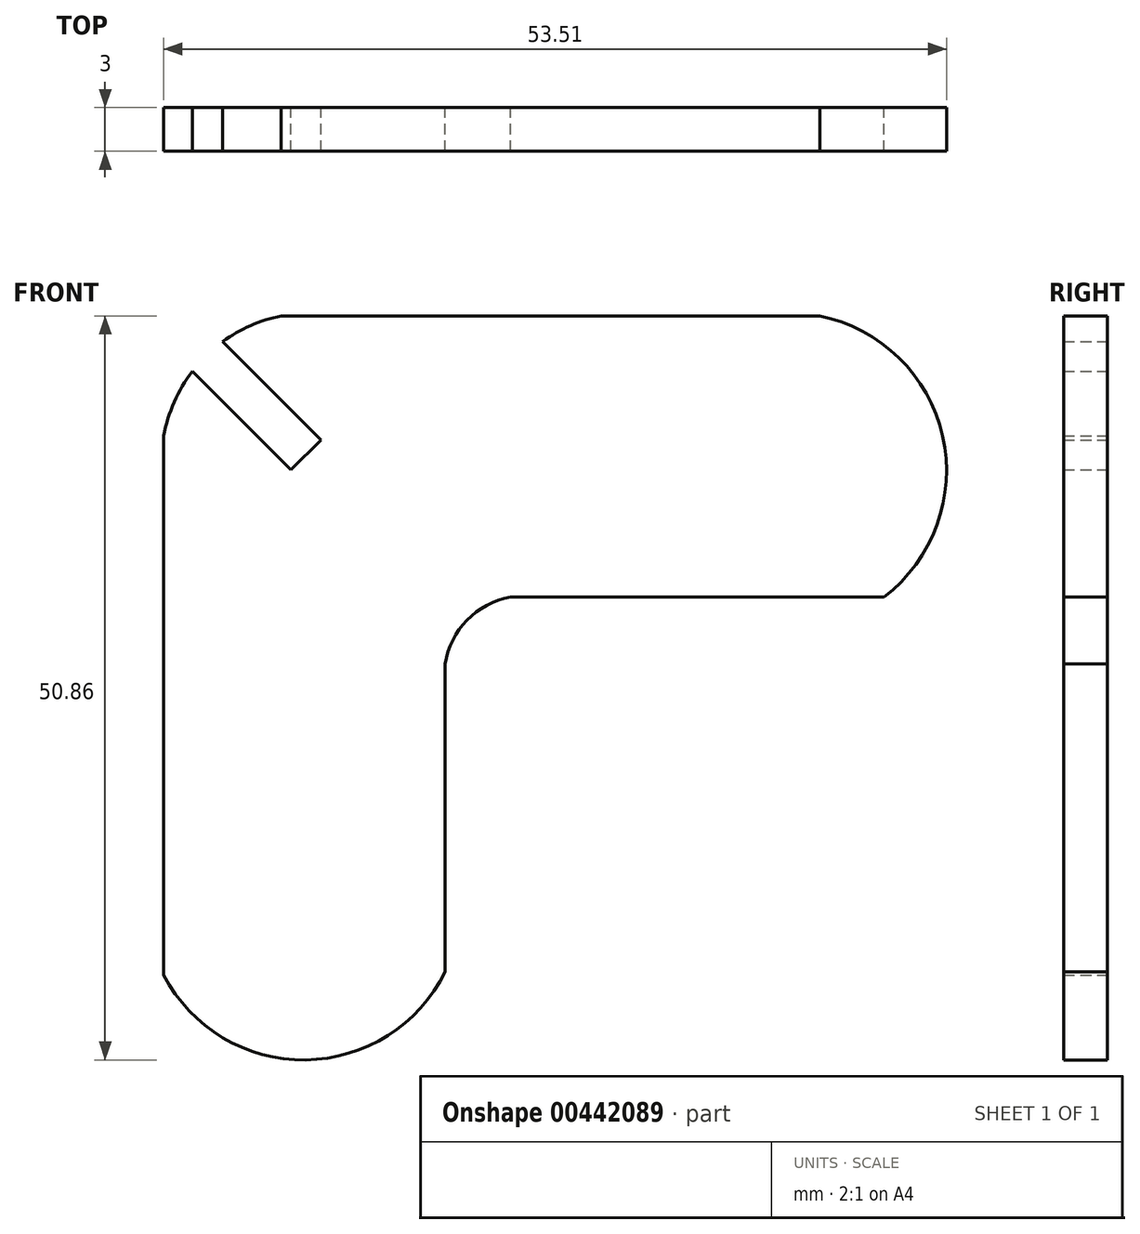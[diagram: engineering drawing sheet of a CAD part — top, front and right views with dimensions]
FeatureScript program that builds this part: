
annotation { "Feature Type Name" : "Feature", "Feature Type Description" : "" }
export const myFeature = defineFeature(function(context is Context, id is Id, definition is map)
    precondition{}
    {
        {
            var Q0;
            Q0=qCreatedBy(makeId("Front.planeOp"),FACE);
            var sketch = newSketch(context, id + "F0", { "sketchPlane" : qUnion([Q0])});
            skLineSegment(sketch, "E0.bottom", {"start": v(-14.18, 20.35) * mm, "end": v(-2.98, 20.35) * mm});
            skLineSegment(sketch, "E0.right", {"start": v(-2.98, 20.35) * mm, "end": v(-2.98, -24.5) * mm});
            skLineSegment(sketch, "E1.bottom", {"start": v(-14.18, 20.35) * mm, "end": v(22.64, 20.35) * mm});
            skLineSegment(sketch, "E1.top", {"start": v(-22.2, 1.12) * mm, "end": v(27.01, 1.12) * mm});
            skLineSegment(sketch, "E1.left", {"start": v(-22.2, 12.14) * mm, "end": v(-22.2, 1.12) * mm});
            skArc(sketch, "E2", {"start": v(-22.2, -24.72) * mm, "mid": v(-12.52, -30.5) * mm, "end": v(-2.98, -24.5) * mm});
            skArc(sketch, "E3", {"start": v(27.01, 1.12) * mm, "mid": v(31.03, 12.15) * mm, "end": v(22.64, 20.35) * mm});
            skPoint(sketch, "E4.middle", {"position": v(-22.2, 20.35) * mm});
            skLineSegment(sketch, "E5", {"start": v(-2.98, 20.35) * mm, "end": v(-22.2, 1.12) * mm});
            skLineSegment(sketch, "E6.bottom", {"start": v(-18.18, 18.6) * mm, "end": v(-0.7, 1.12) * mm});
            skLineSegment(sketch, "E6.top", {"start": v(-20.26, 16.57) * mm, "end": v(-2.98, -0.71) * mm});
            skPoint(sketch, "E6.middle", {"position": v(-14.37, 12.74) * mm});
            skArc(sketch, "E7", {"start": v(-14.18, 20.35) * mm, "mid": v(-16.28, 19.69) * mm, "end": v(-18.18, 18.6) * mm});
            skPoint(sketch, "E6.left.end.orphan", {"position": v(-30.19, 26.5) * mm});
            skPoint(sketch, "E6.left.start.orphan", {"position": v(-28.14, 28.55) * mm});
            skLineSegment(sketch, "E8.trimOffspring", {"start": v(-22.2, 12.14) * mm, "end": v(-22.2, -24.72) * mm});
            skArc(sketch, "E9.trimOffspring", {"start": v(-20.26, 16.57) * mm, "mid": v(-21.5, 14.47) * mm, "end": v(-22.2, 12.14) * mm});
            skPoint(sketch, "E6.right.end.orphan", {"position": v(-0.6, -3.08) * mm});
            skPoint(sketch, "E6.right.start.orphan", {"position": v(1.44, -1.03) * mm});
            skArc(sketch, "E10", {"start": v(3.42, 1.12) * mm, "mid": v(-1.38, -0.36) * mm, "end": v(-2.98, -5.13) * mm});
            skSolve(sketch);
        }
        {
            var Q0;
            {var subQ0=sQuery(id+"F0.wireOp",EDGE,"E2");Q0=makeQuery(id+"F0.imprint","IMPRINT",FACE,{"disambiguationData":[TD([[makeQuery(id+"F0.imprint","IMPRINT",EDGE,{"derivedFrom":subQ0}),1.0]])]});}
            var Q1;
            {var subQ5=sQuery(id+"F0.wireOp",EDGE,"E9.trimOffspring");Q1=makeQuery(id+"F0.imprint","IMPRINT",FACE,{"disambiguationData":[TD([[makeQuery(id+"F0.imprint","IMPRINT",EDGE,{"derivedFrom":subQ5}),1.0]])]});}
            var Q2;
            {var subQ0=sQuery(id+"F0.wireOp",EDGE,"E5");var subQ3=sQuery(id+"F0.wireOp",EDGE,"E6.bottom");var subQ5=makeQuery(id+"F0.imprint","INTERSECT",VERTEX,{"derivedFrom":[subQ0,subQ3]});Q2=makeQuery(id+"F0.imprint","IMPRINT",FACE,{"disambiguationData":[TD([[makeQuery(id+"F0.imprint","IMPRINT",EDGE,{"disambiguationData":[TD([[subQ5,-1.0]])],"derivedFrom":subQ3}),1.0]])]});}
            var Q3;
            {var subQ0=sQuery(id+"F0.wireOp",EDGE,"E5");var subQ3=sQuery(id+"F0.wireOp",EDGE,"E6.top");var subQ5=makeQuery(id+"F0.imprint","INTERSECT",VERTEX,{"derivedFrom":[subQ0,subQ3]});Q3=makeQuery(id+"F0.imprint","IMPRINT",FACE,{"disambiguationData":[TD([[makeQuery(id+"F0.imprint","IMPRINT",EDGE,{"disambiguationData":[TD([[subQ5,-1.0]])],"derivedFrom":subQ3}),-1.0]])]});}
            var Q4;
            {var subQ0=sQuery(id+"F0.wireOp",EDGE,"E3");Q4=makeQuery(id+"F0.imprint","IMPRINT",FACE,{"disambiguationData":[TD([[makeQuery(id+"F0.imprint","IMPRINT",EDGE,{"derivedFrom":subQ0}),1.0]])]});}
            var Q5;
            {var subQ3=sQuery(id+"F0.wireOp",EDGE,"E7");Q5=makeQuery(id+"F0.imprint","IMPRINT",FACE,{"disambiguationData":[TD([[makeQuery(id+"F0.imprint","IMPRINT",EDGE,{"derivedFrom":subQ3}),1.0]])]});}
            var Q6;
            {var subQ0=sQuery(id+"F0.wireOp",EDGE,"E6.bottom");var subQ3=sQuery(id+"F0.wireOp",EDGE,"E0.right");var subQ4=makeQuery(id+"F0.imprint","INTERSECT",VERTEX,{"derivedFrom":[subQ3,subQ0]});Q6=makeQuery(id+"F0.imprint","IMPRINT",FACE,{"disambiguationData":[TD([[makeQuery(id+"F0.imprint","IMPRINT",EDGE,{"disambiguationData":[TD([[subQ4,-1.0]])],"derivedFrom":subQ3}),-1.0]])]});}
            var Q7;
            {var subQ0=sQuery(id+"F0.wireOp",EDGE,"E6.top");var subQ1=sQuery(id+"F0.wireOp",EDGE,"E0.right");var subQ2=makeQuery(id+"F0.imprint","INTERSECT",VERTEX,{"derivedFrom":[subQ1,subQ0]});Q7=makeQuery(id+"F0.imprint","IMPRINT",FACE,{"disambiguationData":[TD([[makeQuery(id+"F0.imprint","IMPRINT",EDGE,{"disambiguationData":[TD([[subQ2,1.0]])],"derivedFrom":subQ1}),-1.0]])]});}
            var Q8;
            {var subQ4=sQuery(id+"F0.wireOp",EDGE,"E0.right");var subQ6=makeQuery(id+"F0.imprint","INTERSECT",VERTEX,{"derivedFrom":[subQ4,sQuery(id+"F0.wireOp",EDGE,"E6.top")]});Q8=makeQuery(id+"F0.imprint","IMPRINT",FACE,{"disambiguationData":[TD([[makeQuery(id+"F0.imprint","IMPRINT",EDGE,{"disambiguationData":[TD([[subQ6,1.0]])],"derivedFrom":subQ4}),1.0]])]});}
            var Q9;
            {var subQ0=sQuery(id+"F0.wireOp",EDGE,"E6.bottom");var subQ1=sQuery(id+"F0.wireOp",EDGE,"E0.right");var subQ2=makeQuery(id+"F0.imprint","INTERSECT",VERTEX,{"derivedFrom":[subQ1,subQ0]});Q9=makeQuery(id+"F0.imprint","IMPRINT",FACE,{"disambiguationData":[TD([[makeQuery(id+"F0.imprint","IMPRINT",EDGE,{"disambiguationData":[TD([[subQ2,-1.0]])],"derivedFrom":subQ1}),1.0]])]});}
            var Q10;
            {var subQ0=sQuery(id+"F0.wireOp",EDGE,"E10");var subQ1=sQuery(id+"F0.wireOp",EDGE,"E0.right");var subQ2=makeQuery(id+"F0.imprint","INTERSECT",VERTEX,{"disambiguationData":[OD(0.0)],"derivedFrom":[subQ1,subQ0]});Q10=makeQuery(id+"F0.imprint","IMPRINT",FACE,{"disambiguationData":[TD([[makeQuery(id+"F0.imprint","IMPRINT",EDGE,{"disambiguationData":[TD([[subQ2,1.0]])],"derivedFrom":subQ1}),-1.0]])]});}
            var Q11;
            {var subQ0=sQuery(id+"F0.wireOp",EDGE,"E10");var subQ1=sQuery(id+"F0.wireOp",EDGE,"E1.top");var subQ2=makeQuery(id+"F0.imprint","INTERSECT",VERTEX,{"disambiguationData":[OD(0.0)],"derivedFrom":[subQ1,subQ0]});Q11=makeQuery(id+"F0.imprint","IMPRINT",FACE,{"disambiguationData":[TD([[makeQuery(id+"F0.imprint","IMPRINT",EDGE,{"disambiguationData":[TD([[subQ2,1.0]])],"derivedFrom":subQ1}),1.0]])]});}
            extrude(context, id + "F1", {"entities" : qUnion([Q0, Q1, Q2, Q3, Q4, Q5, Q6, Q7, Q8, Q9, Q10, Q11]), "depth" : 3 * mm});
        }
    });
